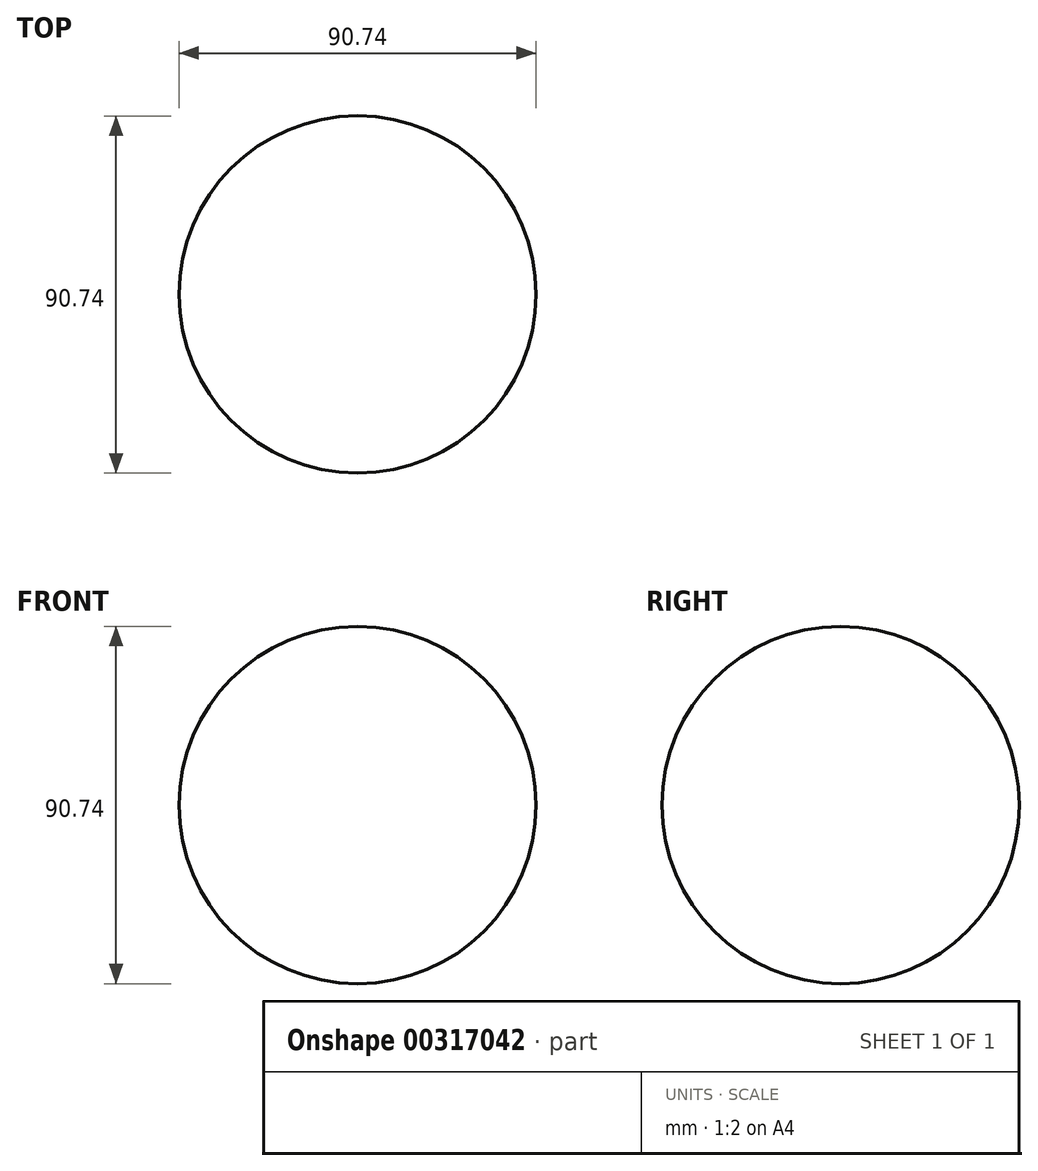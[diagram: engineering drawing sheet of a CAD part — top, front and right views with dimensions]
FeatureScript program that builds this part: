
annotation { "Feature Type Name" : "Feature", "Feature Type Description" : "" }
export const myFeature = defineFeature(function(context is Context, id is Id, definition is map)
    precondition{}
    {
        {
            var Q0;
            Q0=qCreatedBy(makeId("Front.planeOp"),FACE);
            var sketch = newSketch(context, id + "F0", { "sketchPlane" : qUnion([Q0])});
            skArc(sketch, "E0", {"start": v(0, 45.37) * mm, "mid": v(-45.37, 0) * mm, "end": v(0, -45.37) * mm});
            skLineSegment(sketch, "E1", {"start": v(0, 45.37) * mm, "end": v(0, -45.37) * mm});
            skSolve(sketch);
        }
        {
            var Q0;
            Q0 = qSketchRegion(id + "F0", true);
            var Q1;
            Q1=sQuery(id+"F0.wireOp",EDGE,"E1");
            revolve(context, id + "F1", {"entities" : qUnion([Q0]), "axis" : qUnion([Q1]), "revolveType" : RevolveType.FULL});
        }
    });
